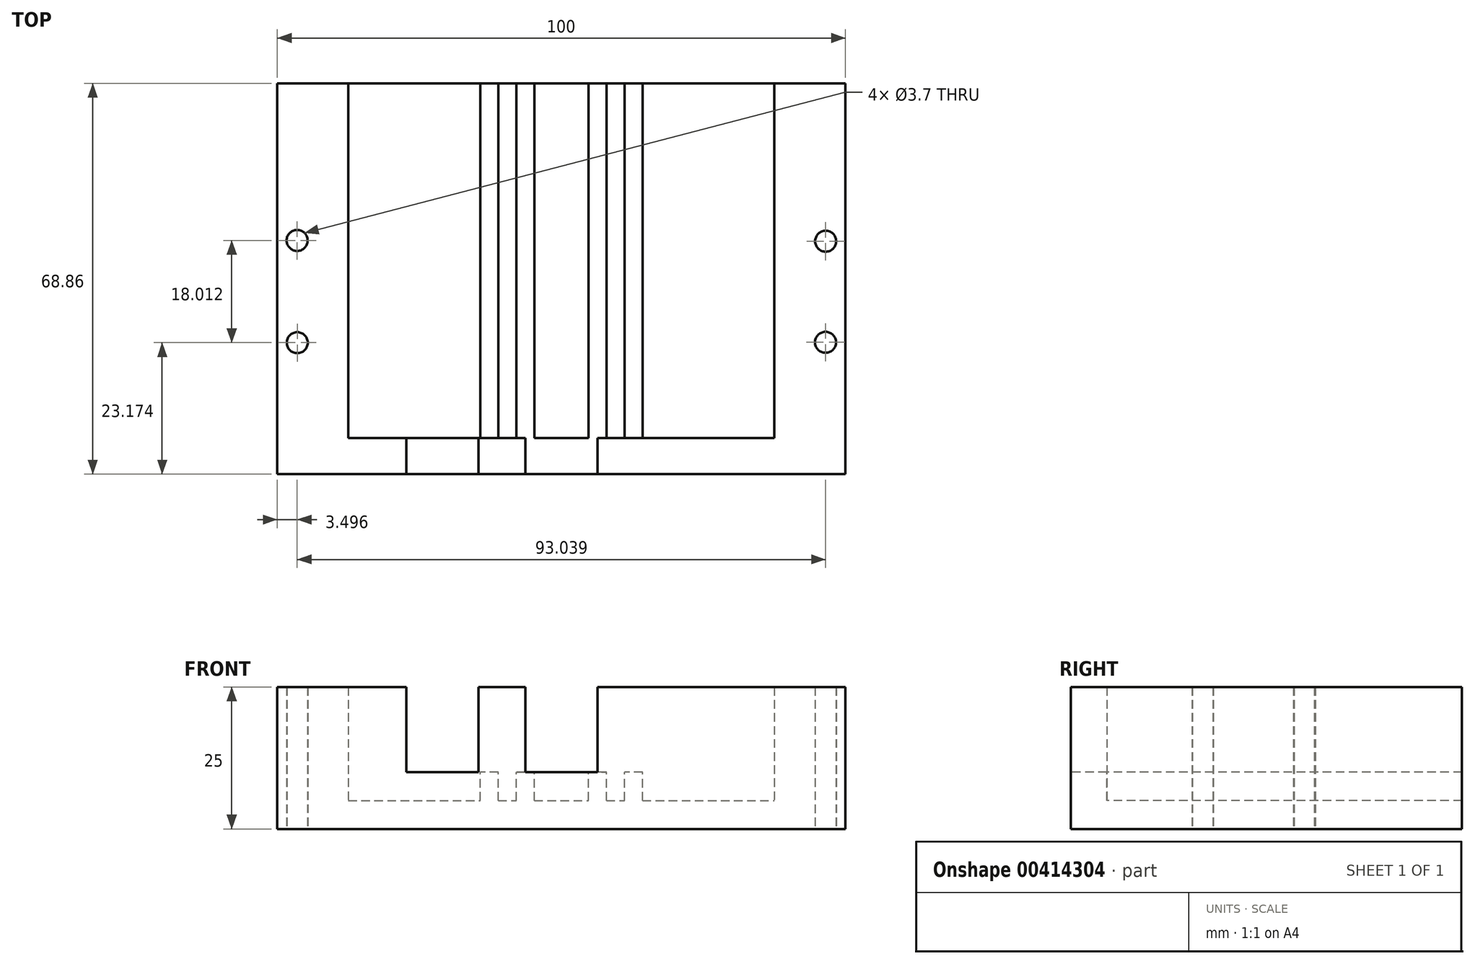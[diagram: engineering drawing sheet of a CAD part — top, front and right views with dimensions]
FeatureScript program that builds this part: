
annotation { "Feature Type Name" : "Feature", "Feature Type Description" : "" }
export const myFeature = defineFeature(function(context is Context, id is Id, definition is map)
    precondition{}
    {
        {
            var Q0;
            Q0=qCreatedBy(makeId("Top.planeOp"),FACE);
            var sketch = newSketch(context, id + "F0", { "sketchPlane" : qUnion([Q0])});
            skLineSegment(sketch, "E0.bottom", {"start": v(-44.9, -50.75) * mm, "end": v(55.1, -50.75) * mm});
            skLineSegment(sketch, "E0.top", {"start": v(-44.9, 18.1) * mm, "end": v(55.1, 18.1) * mm});
            skLineSegment(sketch, "E0.left", {"start": v(-44.9, -50.75) * mm, "end": v(-44.9, 18.1) * mm});
            skLineSegment(sketch, "E0.right", {"start": v(55.1, -50.75) * mm, "end": v(55.1, 18.1) * mm});
            skPoint(sketch, "E1.endSnap0", {"position": v(4.98, -50.77) * mm});
            skSolve(sketch);
        }
        {
            var Q0;
            Q0=qSketchRegion(id+"F0",true);
            extrude(context, id + "F1", {"entities" : qUnion([Q0]), "oppositeDirection" : true, "depth" : 5 * mm});
        }
        {
            var Q0;
            Q0=makeQuery(id+"F1.opExtrude","CAP_FACE",FACE,{"disambiguationData":[OSD([sQuery(id+"F0.wireOp",EDGE,"E0.bottom"),sQuery(id+"F0.wireOp",EDGE,"E0.top"),sQuery(id+"F0.wireOp",EDGE,"E0.left"),sQuery(id+"F0.wireOp",EDGE,"E0.right")])],"isStart":true});
            var sketch = newSketch(context, id + "F2", { "sketchPlane" : qUnion([Q0])});
            skLineSegment(sketch, "E2.left", {"start": v(-34.58, 18.1) * mm, "end": v(-34.58, -50.75) * mm});
            skLineSegment(sketch, "E3.0.4.0", {"start": v(-6, 18.1) * mm, "end": v(-6, -50.75) * mm});
            skLineSegment(sketch, "E3.3.4.0", {"start": v(-9.18, 18.1) * mm, "end": v(-6, 18.1) * mm});
            skLineSegment(sketch, "E3.6.4.0", {"start": v(-9.18, 18.1) * mm, "end": v(-9.18, -50.75) * mm});
            skLineSegment(sketch, "E3.9.4.0", {"start": v(-9.18, -50.75) * mm, "end": v(-6, -50.75) * mm});
            skLineSegment(sketch, "E3.0.5.0", {"start": v(0.34, 18.1) * mm, "end": v(0.34, -50.75) * mm});
            skLineSegment(sketch, "E3.3.5.0", {"start": v(-2.83, 18.1) * mm, "end": v(0.34, 18.1) * mm});
            skLineSegment(sketch, "E3.6.5.0", {"start": v(-2.83, 18.1) * mm, "end": v(-2.83, -50.75) * mm});
            skLineSegment(sketch, "E3.9.5.0", {"start": v(-2.83, -50.75) * mm, "end": v(0.34, -50.75) * mm});
            skLineSegment(sketch, "E3.0.7.0", {"start": v(13.04, 18.1) * mm, "end": v(13.04, -50.75) * mm});
            skLineSegment(sketch, "E3.3.7.0", {"start": v(9.87, 18.1) * mm, "end": v(13.04, 18.1) * mm});
            skLineSegment(sketch, "E3.6.7.0", {"start": v(9.87, 18.1) * mm, "end": v(9.87, -50.75) * mm});
            skLineSegment(sketch, "E3.9.7.0", {"start": v(9.87, -50.75) * mm, "end": v(13.04, -50.75) * mm});
            skLineSegment(sketch, "E3.0.8.0", {"start": v(19.4, 18.1) * mm, "end": v(19.4, -50.75) * mm});
            skLineSegment(sketch, "E3.3.8.0", {"start": v(16.22, 18.1) * mm, "end": v(19.4, 18.1) * mm});
            skLineSegment(sketch, "E3.6.8.0", {"start": v(16.22, 18.1) * mm, "end": v(16.22, -50.75) * mm});
            skLineSegment(sketch, "E3.9.8.0", {"start": v(16.22, -50.75) * mm, "end": v(19.4, -50.75) * mm});
            skLineSegment(sketch, "E3.0.12.0", {"start": v(44.8, 18.1) * mm, "end": v(44.8, -50.75) * mm});
            skSolve(sketch);
        }
        {
            var Q0;
            Q0=qSketchRegion(id+"F2",true);
            extrude(context, id + "F3", {"entities" : qUnion([Q0]), "operationType" : NewBodyOperationType.ADD, "depth" : 5 * mm});
        }
        {
            var Q0;
            {var subQ0=sQuery(id+"F0.wireOp",EDGE,"E0.bottom");var subQ1=sQuery(id+"F0.wireOp",EDGE,"E0.top");var subQ2=sQuery(id+"F0.wireOp",EDGE,"E0.left");Q0=makeQuery(id+"F3.boolean.opBoolean","SPLIT",FACE,{"disambiguationData":[TD([makeQuery(id+"F1.opExtrude","SWEPT_FACE",FACE,{"disambiguationData":[OSD([subQ2])]})])],"derivedFrom":makeQuery(id+"F1.opExtrude","CAP_FACE",FACE,{"disambiguationData":[OSD([subQ0,subQ1,subQ2,sQuery(id+"F0.wireOp",EDGE,"E0.right")])],"isStart":true})});}
            var sketch = newSketch(context, id + "F4", { "sketchPlane" : qUnion([Q0])});
            skLineSegment(sketch, "E4.bottom", {"start": v(-44.9, 18.1) * mm, "end": v(-32.4, 18.1) * mm});
            skLineSegment(sketch, "E4.top", {"start": v(-44.9, -50.75) * mm, "end": v(-32.4, -50.75) * mm});
            skLineSegment(sketch, "E4.left", {"start": v(-44.9, 18.1) * mm, "end": v(-44.9, -50.75) * mm});
            skLineSegment(sketch, "E4.right", {"start": v(-32.4, 18.1) * mm, "end": v(-32.4, -50.75) * mm});
            skPoint(sketch, "E5", {"position": v(55.1, 18.1) * mm});
            skLineSegment(sketch, "E6.bottom", {"start": v(55.1, 18.1) * mm, "end": v(42.6, 18.1) * mm});
            skLineSegment(sketch, "E6.top", {"start": v(55.1, -50.75) * mm, "end": v(42.6, -50.75) * mm});
            skLineSegment(sketch, "E6.left", {"start": v(55.1, 18.1) * mm, "end": v(55.1, -50.75) * mm});
            skLineSegment(sketch, "E6.right", {"start": v(42.6, 18.1) * mm, "end": v(42.6, -50.75) * mm});
            skPoint(sketch, "E7", {"position": v(-44.9, -50.75) * mm});
            skLineSegment(sketch, "E8.bottom", {"start": v(-44.9, -50.75) * mm, "end": v(55.1, -50.75) * mm});
            skLineSegment(sketch, "E8.top", {"start": v(-44.9, -44.4) * mm, "end": v(55.1, -44.4) * mm});
            skLineSegment(sketch, "E8.left", {"start": v(-44.9, -50.75) * mm, "end": v(-44.9, -44.4) * mm});
            skLineSegment(sketch, "E8.right", {"start": v(55.1, -50.75) * mm, "end": v(55.1, -44.4) * mm});
            skPoint(sketch, "E9", {"position": v(-44.9, 18.1) * mm});
            skSolve(sketch);
        }
        {
            var Q0;
            Q0=qSketchRegion(id+"F4",true);
            extrude(context, id + "F5", {"entities" : qUnion([Q0]), "operationType" : NewBodyOperationType.ADD, "depth" : 20 * mm});
        }
        {
            var Q0;
            Q0=makeQuery(id+"F1.boolean.opBoolean","MERGE",FACE,{"derivedFrom":[makeQuery(id+"FrM0S1BdwquSU4h_1.opExtrude","CAP_FACE",FACE,{"disambiguationData":[OSD([sQuery(id+"F1paRBLzH6P92U9_1.wireOp",EDGE,"ca1a8222-2888-463a-b1ca-637cd0208124.0"),sQuery(id+"F1paRBLzH6P92U9_1.wireOp",EDGE,"ca1a8222-2888-463a-b1ca-637cd0208124.1"),sQuery(id+"F1paRBLzH6P92U9_1.wireOp",EDGE,"ca1a8222-2888-463a-b1ca-637cd0208124.2"),sQuery(id+"F1paRBLzH6P92U9_1.wireOp",EDGE,"ca1a8222-2888-463a-b1ca-637cd0208124.3")])],"isStart":true}),makeQuery(id+"F1.opExtrude","CAP_FACE",FACE,{"disambiguationData":[OSD([sQuery(id+"F0.wireOp",EDGE,"E0.bottom"),sQuery(id+"F0.wireOp",EDGE,"E0.top"),sQuery(id+"F0.wireOp",EDGE,"E0.left"),sQuery(id+"F0.wireOp",EDGE,"E0.right")])],"isStart":false})]});
            var sketch = newSketch(context, id + "F6", { "sketchPlane" : qUnion([Q0])});
            skCircle(sketch, "E10", {"center": v(-41.39, 27.58) * mm, "radius": 1.85 * mm});
            skCircle(sketch, "E11", {"center": v(51.6, 27.51) * mm, "radius": 1.85 * mm});
            skLineSegment(sketch, "E12", {"start": v(-44.9, 50.75) * mm, "end": v(-41.4, 50.75) * mm});
            skCircle(sketch, "E13", {"center": v(-41.41, 9.56) * mm, "radius": 1.85 * mm});
            skCircle(sketch, "E14", {"center": v(51.62, 9.7) * mm, "radius": 1.85 * mm});
            skSolve(sketch);
        }
        {
            var Q0;
            Q0=qSketchRegion(id+"F6",true);
            extrude(context, id + "F7", {"entities" : qUnion([Q0]), "operationType" : NewBodyOperationType.REMOVE, "endBound" : BoundingType.THROUGH_ALL, "oppositeDirection" : true, "depth" : 25.4 * mm});
        }
        {
            var Q0;
            Q0=makeQuery(id+"F5.boolean.opBoolean","MERGE",FACE,{"derivedFrom":[makeQuery(id+"F3.boolean.opBoolean","MERGE",FACE,{"derivedFrom":[makeQuery(id+"F1.opExtrude","SWEPT_FACE",FACE,{"disambiguationData":[OSD([sQuery(id+"F0.wireOp",EDGE,"E0.bottom")])]}),makeQuery(id+"F3.opExtrude","SWEPT_FACE",FACE,{"disambiguationData":[OSD([sQuery(id+"F2.wireOp",EDGE,"E2.top")])]}),makeQuery(id+"F3.opExtrude","SWEPT_FACE",FACE,{"disambiguationData":[OSD([sQuery(id+"F2.wireOp",EDGE,"b44929e1-93cd-42a0-b5ec-e1a20ae832c9.1.0.3")])]}),makeQuery(id+"F3.opExtrude","SWEPT_FACE",FACE,{"disambiguationData":[OSD([sQuery(id+"F2.wireOp",EDGE,"b44929e1-93cd-42a0-b5ec-e1a20ae832c9.2.0.3")])]}),makeQuery(id+"F3.opExtrude","SWEPT_FACE",FACE,{"disambiguationData":[OSD([sQuery(id+"F2.wireOp",EDGE,"E3.9.3.0")])]}),makeQuery(id+"F3.opExtrude","SWEPT_FACE",FACE,{"disambiguationData":[OSD([sQuery(id+"F2.wireOp",EDGE,"E3.9.4.0")])]}),makeQuery(id+"F3.opExtrude","SWEPT_FACE",FACE,{"disambiguationData":[OSD([sQuery(id+"F2.wireOp",EDGE,"E3.9.5.0")])]}),makeQuery(id+"F3.opExtrude","SWEPT_FACE",FACE,{"disambiguationData":[OSD([sQuery(id+"F2.wireOp",EDGE,"E3.9.7.0")])]}),makeQuery(id+"F3.opExtrude","SWEPT_FACE",FACE,{"disambiguationData":[OSD([sQuery(id+"F2.wireOp",EDGE,"E3.9.8.0")])]}),makeQuery(id+"F3.opExtrude","SWEPT_FACE",FACE,{"disambiguationData":[OSD([sQuery(id+"F2.wireOp",EDGE,"E3.9.9.0")])]}),makeQuery(id+"F3.opExtrude","SWEPT_FACE",FACE,{"disambiguationData":[OSD([sQuery(id+"F2.wireOp",EDGE,"E3.9.10.0")])]}),makeQuery(id+"F3.opExtrude","SWEPT_FACE",FACE,{"disambiguationData":[OSD([sQuery(id+"F2.wireOp",EDGE,"E3.9.11.0")])]}),makeQuery(id+"F3.opExtrude","SWEPT_FACE",FACE,{"disambiguationData":[OSD([sQuery(id+"F2.wireOp",EDGE,"E3.9.12.0")])]})]}),makeQuery(id+"F5.opExtrude","SWEPT_FACE",FACE,{"disambiguationData":[OSD([sQuery(id+"F4.wireOp",EDGE,"E8.bottom")])]})]});
            var sketch = newSketch(context, id + "F8", { "sketchPlane" : qUnion([Q0])});
            skLineSegment(sketch, "E15", {"start": v(5.1, 5) * mm, "end": v(-1.26, 5) * mm});
            skLineSegment(sketch, "E16", {"start": v(5.1, 5) * mm, "end": v(11.44, 5) * mm});
            skLineSegment(sketch, "E17", {"start": v(11.44, 5) * mm, "end": v(11.44, 20) * mm});
            skLineSegment(sketch, "E18", {"start": v(-1.26, 5) * mm, "end": v(-1.26, 20) * mm});
            skLineSegment(sketch, "E19", {"start": v(-1.26, 20) * mm, "end": v(11.44, 20) * mm});
            skLineSegment(sketch, "E20.bottom", {"start": v(-1.26, 5) * mm, "end": v(11.44, 5) * mm});
            skLineSegment(sketch, "E20.top", {"start": v(-1.26, 5) * mm, "end": v(11.44, 5) * mm});
            skLineSegment(sketch, "E20.left", {"start": v(-1.26, 5) * mm, "end": v(-1.26, 5) * mm});
            skLineSegment(sketch, "E20.right", {"start": v(11.44, 5) * mm, "end": v(11.44, 5) * mm});
            skLineSegment(sketch, "E21", {"start": v(-22.21, 5) * mm, "end": v(-22.21, 20) * mm});
            skLineSegment(sketch, "E22", {"start": v(-22.21, 5) * mm, "end": v(-9.51, 5) * mm});
            skLineSegment(sketch, "E23", {"start": v(-9.51, 5) * mm, "end": v(-9.51, 20) * mm});
            skLineSegment(sketch, "E24", {"start": v(-9.51, 20) * mm, "end": v(-22.21, 20) * mm});
            skSolve(sketch);
        }
        {
            var Q0;
            Q0=qSketchRegion(id+"F8",true);
            extrude(context, id + "F9", {"entities" : qUnion([Q0]), "operationType" : NewBodyOperationType.REMOVE, "oppositeDirection" : true, "depth" : 12.7 * mm});
        }
    });
